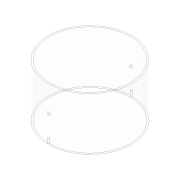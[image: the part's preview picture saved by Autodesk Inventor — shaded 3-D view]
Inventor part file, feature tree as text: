
AUTODESK INVENTOR PART (.ipt)
format: ipt  version: 2018 (Build 220112000, 112)  size: 120,832 bytes
history: native  units: mm
features: extrude x4, sketch x4, pattern_circular x1
ambient origin geometry x8: Origin, YZ Plane, XZ Plane, XY Plane, X Axis, Y Axis, Z Axis, Center Point
bodies: Solid1 (feature_tree)
feature tree (9):
  extrude  "Extrusion1"  Depth=2.0mm
  extrude  "Extrusion2"  Depth=10.0mm TaperAngle=0.0deg
  extrude  "Extrusion3"  Depth=10.0mm TaperAngle=0.0deg
  extrude  "Extrusion5"  Depth=39.6875mm
  pattern_circular  "Circular Pattern2"  [2 undecoded]
  sketch  "Sketch1"  dims[d0=76.2mm d1=79.375mm d2=50.0mm d3=0.0mm d4=2.0mm]
  sketch  "Sketch2"  dims[d5=30.0mm d6=10.0mm d7=0.0mm]
  sketch  "Sketch3"  dims[d8=2.0mm d10=10.0mm d11=0.0mm]
  sketch  "Sketch5"  dims[d12=25.0mm d20=2.0mm d21=39.6875mm d22=5.0mm d23=0.0mm d24=20.0mm d25=360.0deg]
note: 2 required parameter values undecoded (feature->parameter linkage not recoverable at this tier; creation-order binding heuristic only, values carry confidence <= 0.55)
